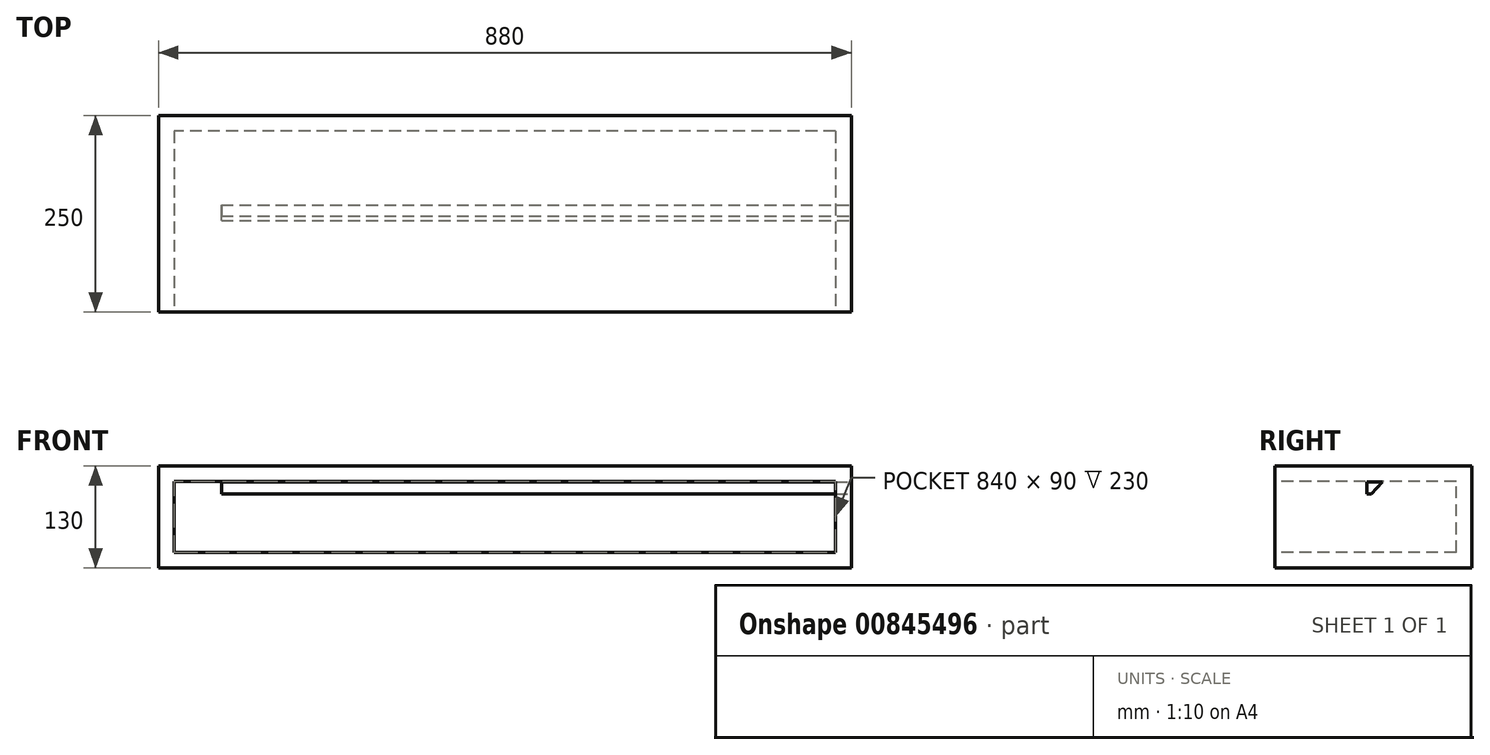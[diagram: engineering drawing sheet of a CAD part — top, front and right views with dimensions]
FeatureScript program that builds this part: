
annotation { "Feature Type Name" : "Feature", "Feature Type Description" : "" }
export const myFeature = defineFeature(function(context is Context, id is Id, definition is map)
    precondition{}
    {
        {
            var Q0;
            Q0=qCreatedBy(makeId("Front.planeOp"),FACE);
            var sketch = newSketch(context, id + "F0", { "sketchPlane" : qUnion([Q0])});
            skLineSegment(sketch, "E0.bottom", {"start": v(440, -65) * mm, "end": v(-440, -65) * mm});
            skLineSegment(sketch, "E0.top", {"start": v(440, 65) * mm, "end": v(-440, 65) * mm});
            skLineSegment(sketch, "E0.left", {"start": v(440, -65) * mm, "end": v(440, 65) * mm});
            skLineSegment(sketch, "E0.right", {"start": v(-440, -65) * mm, "end": v(-440, 65) * mm});
            skPoint(sketch, "E0.middle", {"position": v(0, 0) * mm});
            skSolve(sketch);
        }
        {
            var Q0;
            Q0=qSketchRegion(id+"F0",true);
            extrude(context, id + "F1", {"entities" : qUnion([Q0]), "depth" : 250 * mm});
        }
        {
            var Q0;
            Q0=makeQuery(id+"F1.opExtrude","CAP_FACE",FACE,{"disambiguationData":[OSD([sQuery(id+"F0.wireOp",EDGE,"E0.bottom"),sQuery(id+"F0.wireOp",EDGE,"E0.top"),sQuery(id+"F0.wireOp",EDGE,"E0.left"),sQuery(id+"F0.wireOp",EDGE,"E0.right")])],"isStart":false});
            var sketch = newSketch(context, id + "F2", { "sketchPlane" : qUnion([Q0])});
            skLineSegment(sketch, "E1.bottom", {"start": v(420, -45) * mm, "end": v(-420, -45) * mm});
            skLineSegment(sketch, "E1.top", {"start": v(420, 45) * mm, "end": v(-420, 45) * mm});
            skLineSegment(sketch, "E1.left", {"start": v(420, -45) * mm, "end": v(420, 45) * mm});
            skLineSegment(sketch, "E1.right", {"start": v(-420, -45) * mm, "end": v(-420, 45) * mm});
            skPoint(sketch, "E1.middle", {"position": v(0, 0) * mm});
            skSolve(sketch);
        }
        {
            var Q0;
            Q0=qSketchRegion(id+"F2",true);
            extrude(context, id + "F3", {"entities" : qUnion([Q0]), "operationType" : NewBodyOperationType.REMOVE, "oppositeDirection" : true, "depth" : 230 * mm});
        }
        {
            var Q0;
            Q0=makeQuery(id+"F1.opExtrude","SWEPT_FACE",FACE,{"disambiguationData":[OSD([sQuery(id+"F0.wireOp",EDGE,"E0.left")])]});
            var sketch = newSketch(context, id + "F4", { "sketchPlane" : qUnion([Q0])});
            skLineSegment(sketch, "E2", {"start": v(-113.7, 44.18) * mm, "end": v(-133.7, 44.18) * mm});
            skLineSegment(sketch, "E3", {"start": v(-133.7, 44.18) * mm, "end": v(-133.7, 29.18) * mm});
            skLineSegment(sketch, "E4", {"start": v(-133.7, 29.18) * mm, "end": v(-127.7, 29.18) * mm});
            skLineSegment(sketch, "E5", {"start": v(-127.7, 29.18) * mm, "end": v(-113.7, 44.18) * mm});
            skSolve(sketch);
        }
        {
            var Q0;
            Q0 = qSketchRegion(id + "F4", true);
            extrude(context, id + "F5", {"entities" : qUnion([Q0]), "oppositeDirection" : true, "depth" : 800 * mm, "offsetDistance" : 25 * mm});
        }
    });
